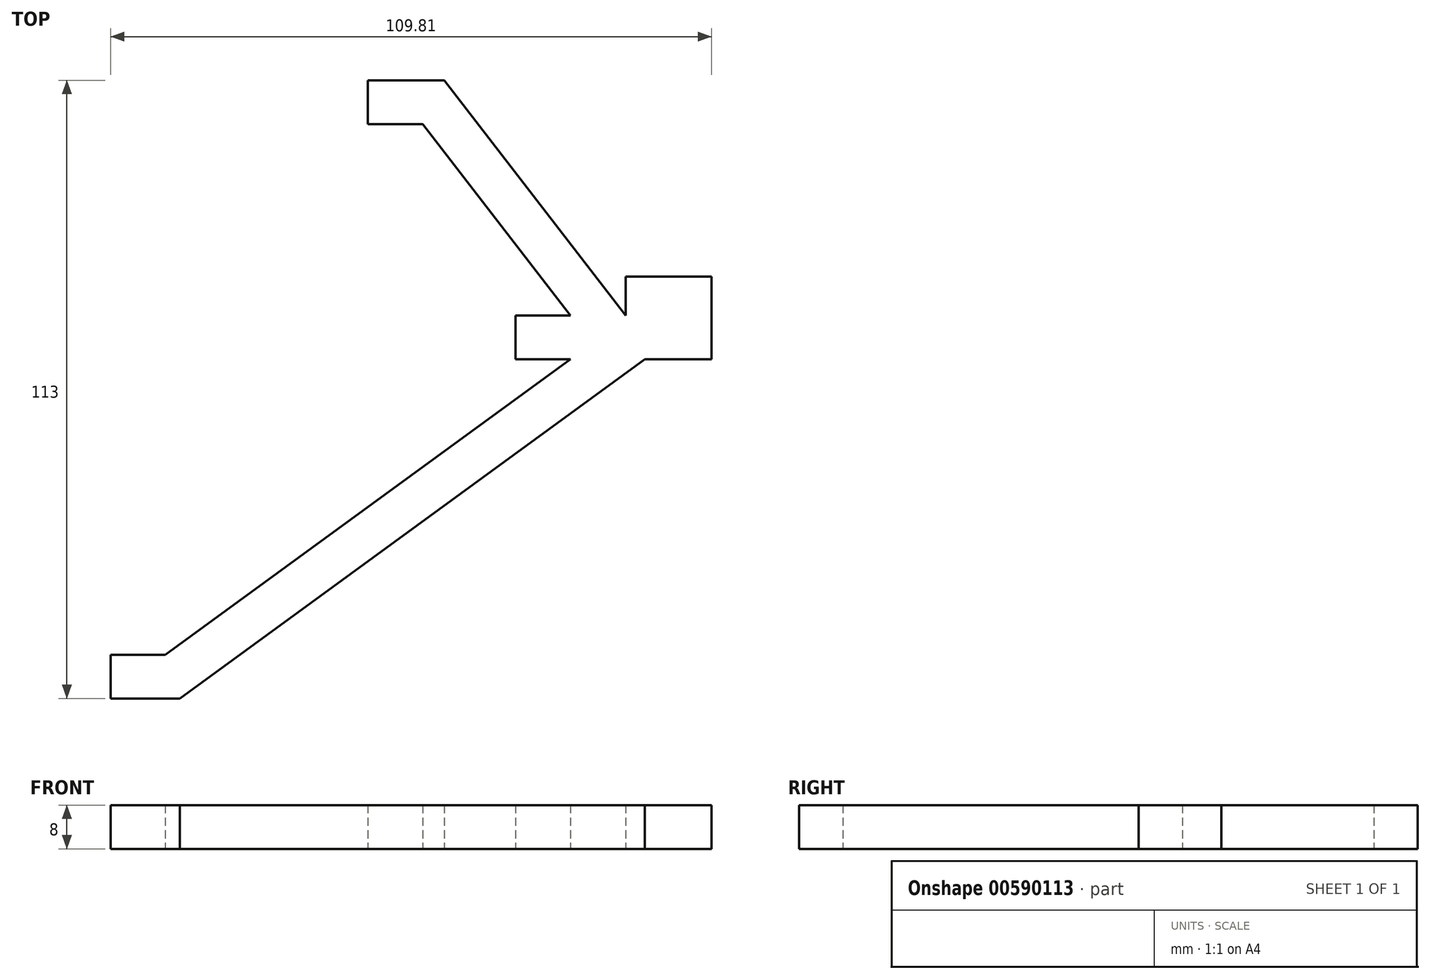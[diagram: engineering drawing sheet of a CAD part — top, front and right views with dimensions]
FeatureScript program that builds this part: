
annotation { "Feature Type Name" : "Feature", "Feature Type Description" : "" }
export const myFeature = defineFeature(function(context is Context, id is Id, definition is map)
    precondition{}
    {
        {
            var Q0;
            Q0=qCreatedBy(makeId("Top.planeOp"),FACE);
            var sketch = newSketch(context, id + "F0", { "sketchPlane" : qUnion([Q0])});
            skLineSegment(sketch, "E0", {"start": v(0, 4) * mm, "end": v(10, 4) * mm});
            skLineSegment(sketch, "E1", {"start": v(-17, 39) * mm, "end": v(-27, 39) * mm});
            skLineSegment(sketch, "E2", {"start": v(-27, 39) * mm, "end": v(-17, 39) * mm});
            skLineSegment(sketch, "E3", {"start": v(10, 4) * mm, "end": v(-17, 39) * mm});
            skLineSegment(sketch, "E4", {"start": v(0, 4) * mm, "end": v(0, -4) * mm});
            skLineSegment(sketch, "E5", {"start": v(0, -4) * mm, "end": v(10, -4) * mm});
            skLineSegment(sketch, "E6", {"start": v(10, -4) * mm, "end": v(-64, -58) * mm});
            skLineSegment(sketch, "E7", {"start": v(-64, -58) * mm, "end": v(-74, -58) * mm});
            skLineSegment(sketch, "E8", {"start": v(-74, -58) * mm, "end": v(-74, -66) * mm});
            skLineSegment(sketch, "E9", {"start": v(-74, -66) * mm, "end": v(-61.4, -66) * mm});
            skLineSegment(sketch, "E10", {"start": v(-61.4, -66) * mm, "end": v(23.57, -4) * mm});
            skLineSegment(sketch, "E11", {"start": v(23.57, -4) * mm, "end": v(35.8, -4) * mm});
            skLineSegment(sketch, "E12", {"start": v(35.8, -4) * mm, "end": v(35.8, 11.15) * mm});
            skLineSegment(sketch, "E13", {"start": v(35.8, 11.15) * mm, "end": v(20.1, 11.15) * mm});
            skLineSegment(sketch, "E14", {"start": v(20.1, 11.15) * mm, "end": v(20.1, 4) * mm});
            skLineSegment(sketch, "E15", {"start": v(20.1, 4) * mm, "end": v(-13.07, 47) * mm});
            skLineSegment(sketch, "E16", {"start": v(-13.07, 47) * mm, "end": v(-27, 47) * mm});
            skLineSegment(sketch, "E17", {"start": v(-27, 47) * mm, "end": v(-27, 39) * mm});
            skLineSegment(sketch, "E18", {"start": v(-27, 43) * mm, "end": v(27.22, 43) * mm, "construction": true});
            skLineSegment(sketch, "E19", {"start": v(-74, -62) * mm, "end": v(30.15, -62) * mm, "construction": true});
            skLineSegment(sketch, "E20", {"start": v(0, 0) * mm, "end": v(49.8, 0) * mm, "construction": true});
            skSolve(sketch);
        }
        {
            var Q0;
            Q0=makeQuery(id+"F0.imprint","IMPRINT",FACE,{"disambiguationData":[TD([[makeQuery(id+"F0.imprint","IMPRINT",EDGE,{"derivedFrom":sQuery(id+"F0.wireOp",EDGE,"E0")}),-1.0]])]});
            extrude(context, id + "F1", {"entities" : qUnion([Q0]), "depth" : 8 * mm, "offsetDistance" : 25 * mm});
        }
    });
